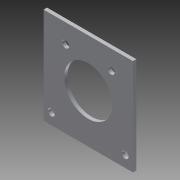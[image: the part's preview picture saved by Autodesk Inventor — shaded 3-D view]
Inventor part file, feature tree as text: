
AUTODESK INVENTOR PART (.ipt)
format: ipt  version: 2013 (Build 170138000, 138)  size: 123,392 bytes
history: native  units: in
note: dims shown in document units (in); Inventor stores cm internally (conversion verified against a paired STEP export)
features: reference x7, sketch x3, other x3, sheet_metal_op x1
ambient origin geometry x8: Origin, YZ Plane, XZ Plane, XY Plane, X Axis, Y Axis, Z Axis, Center Point
feature tree (14):
  sheet_metal_op  "Face2"
  sketch  "Sketch7"  dims[d1=2.244in]
  other  "Plate5"
  sketch  "Sketch11"  dims[d2=3.5in]
  reference  "Reference5"
  reference  "Reference6"
  reference  "Reference7"
  reference  "Reference8"
  reference  "Reference9"
  reference  "Reference10"
  reference  "Reference11"
  sketch  "Sketch12"  dims[d3=0.295in d4=0.25in d5=0.295in d8=0.125in d19=0.25in d48=0.5in d56=0.125in d57=0.5in d69=0.125in d70=0.0in d71=1.75in d72=0.125in d73=0.0in]
  other  "Cut5"
  other  "Cut6"
